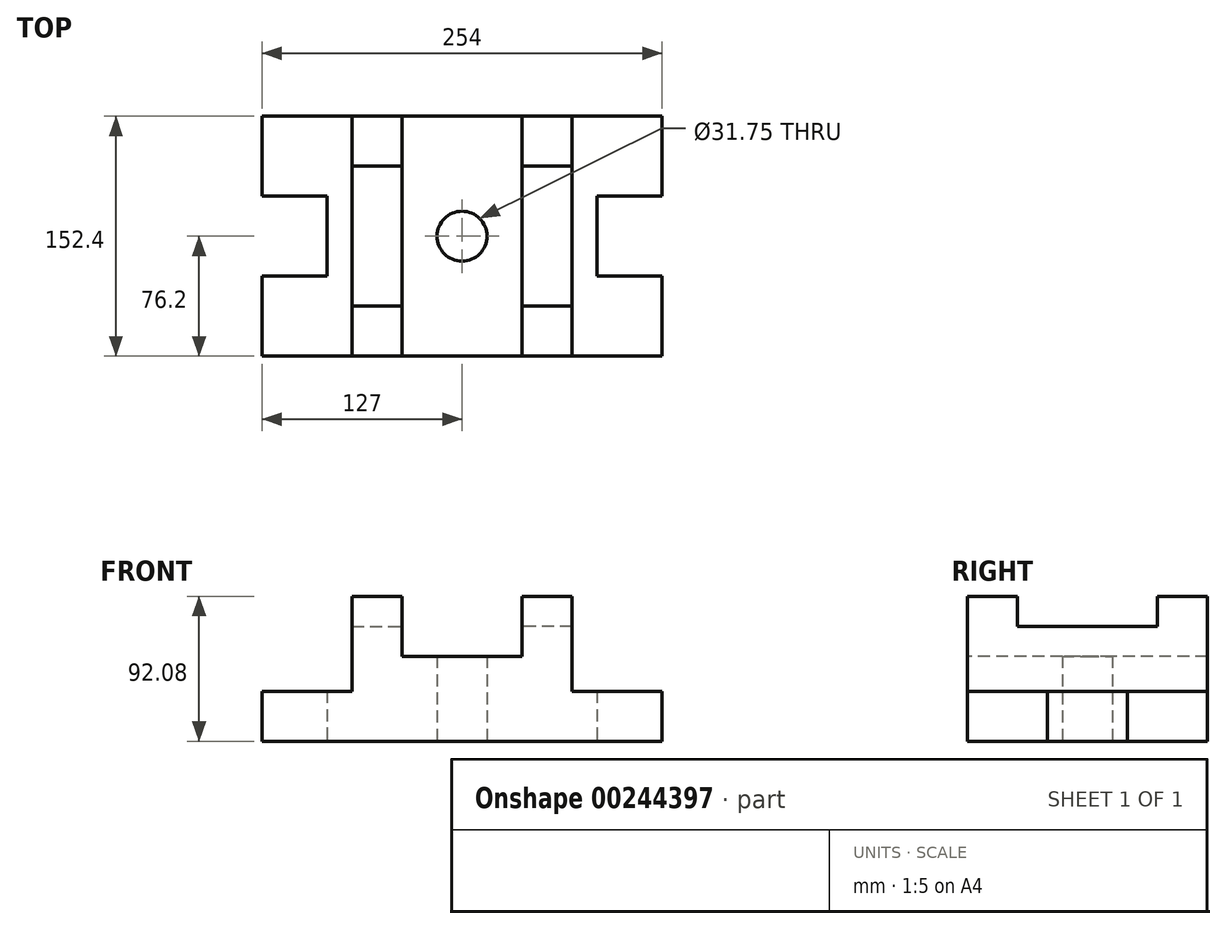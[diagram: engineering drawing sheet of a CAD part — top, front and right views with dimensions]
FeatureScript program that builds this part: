
annotation { "Feature Type Name" : "Feature", "Feature Type Description" : "" }
export const myFeature = defineFeature(function(context is Context, id is Id, definition is map)
    precondition{}
    {
        {
            var Q0;
            Q0=qCreatedBy(makeId("Top.planeOp"),FACE);
            var sketch = newSketch(context, id + "F0", { "sketchPlane" : qUnion([Q0])});
            skCircle(sketch, "E0", {"center": v(0, 0) * mm, "radius": 15.88 * mm});
            skLineSegment(sketch, "E1", {"start": v(0, 0) * mm, "end": v(0, -76.2) * mm});
            skLineSegment(sketch, "E2", {"start": v(0, -76.2) * mm, "end": v(127, -76.2) * mm});
            skLineSegment(sketch, "E3", {"start": v(127, -76.2) * mm, "end": v(127, -25.4) * mm});
            skLineSegment(sketch, "E4", {"start": v(127, -25.4) * mm, "end": v(85.72, -25.4) * mm});
            skLineSegment(sketch, "E5", {"start": v(85.72, -25.4) * mm, "end": v(85.72, 25.4) * mm});
            skLineSegment(sketch, "E6.MirrorCS", {"start": v(-85.72, -25.4) * mm, "end": v(-85.72, 25.4) * mm});
            skLineSegment(sketch, "E7.MirrorCS", {"start": v(-127, -76.2) * mm, "end": v(-127, -25.4) * mm});
            skLineSegment(sketch, "E8.MirrorCS", {"start": v(-127, -25.4) * mm, "end": v(-85.72, -25.4) * mm});
            skLineSegment(sketch, "E9.MirrorCS", {"start": v(0, -76.2) * mm, "end": v(-127, -76.2) * mm});
            skLineSegment(sketch, "E10.MirrorCS", {"start": v(-127, 25.4) * mm, "end": v(-85.72, 25.4) * mm});
            skLineSegment(sketch, "E11.MirrorCS", {"start": v(-127, 76.2) * mm, "end": v(-127, 25.4) * mm});
            skLineSegment(sketch, "E12.MirrorCS", {"start": v(0, 76.2) * mm, "end": v(-127, 76.2) * mm});
            skLineSegment(sketch, "E13.MirrorCS", {"start": v(0, 76.2) * mm, "end": v(127, 76.2) * mm});
            skLineSegment(sketch, "E14.MirrorCS", {"start": v(127, 76.2) * mm, "end": v(127, 25.4) * mm});
            skLineSegment(sketch, "E15.MirrorCS", {"start": v(127, 25.4) * mm, "end": v(85.72, 25.4) * mm});
            skLineSegment(sketch, "E16", {"start": v(-127, 76.2) * mm, "end": v(-69.85, 76.2) * mm});
            skLineSegment(sketch, "E17", {"start": v(-69.85, 76.2) * mm, "end": v(-69.85, 44.45) * mm});
            skLineSegment(sketch, "E18", {"start": v(-69.85, 44.45) * mm, "end": v(-38.1, 44.45) * mm});
            skLineSegment(sketch, "E19", {"start": v(-38.1, 44.45) * mm, "end": v(-38.1, 76.2) * mm});
            skLineSegment(sketch, "E20.MirrorCS", {"start": v(38.1, 44.45) * mm, "end": v(38.1, 76.2) * mm});
            skLineSegment(sketch, "E21.MirrorCS", {"start": v(69.85, 44.45) * mm, "end": v(38.1, 44.45) * mm});
            skLineSegment(sketch, "E22.MirrorCS", {"start": v(69.85, 76.2) * mm, "end": v(69.85, 44.45) * mm});
            skLineSegment(sketch, "E23.MirrorCS", {"start": v(69.85, -44.45) * mm, "end": v(38.1, -44.45) * mm});
            skLineSegment(sketch, "E24.MirrorCS", {"start": v(38.1, -44.45) * mm, "end": v(38.1, -76.2) * mm});
            skLineSegment(sketch, "E25.MirrorCS", {"start": v(69.85, -76.2) * mm, "end": v(69.85, -44.45) * mm});
            skLineSegment(sketch, "E26.MirrorCS", {"start": v(-38.1, -44.45) * mm, "end": v(-38.1, -76.2) * mm});
            skLineSegment(sketch, "E27.MirrorCS", {"start": v(-69.85, -44.45) * mm, "end": v(-38.1, -44.45) * mm});
            skLineSegment(sketch, "E28.MirrorCS", {"start": v(-69.85, -76.2) * mm, "end": v(-69.85, -44.45) * mm});
            skLineSegment(sketch, "E29", {"start": v(-69.85, 44.45) * mm, "end": v(-69.85, -44.45) * mm});
            skLineSegment(sketch, "E30", {"start": v(-38.1, 44.45) * mm, "end": v(-38.1, -44.45) * mm});
            skLineSegment(sketch, "E31", {"start": v(38.1, 44.45) * mm, "end": v(38.1, -44.45) * mm});
            skLineSegment(sketch, "E32", {"start": v(69.85, -44.45) * mm, "end": v(69.85, 44.45) * mm});
            skSolve(sketch);
        }
        {
            var Q0;
            Q0=makeQuery(id+"F0.imprint","IMPRINT",FACE,{"disambiguationData":[TD([[makeQuery(id+"F0.imprint","IMPRINT",EDGE,{"derivedFrom":sQuery(id+"F0.wireOp",EDGE,"E23.MirrorCS")}),1.0]])]});
            var Q1;
            {var subQ0=sQuery(id+"F0.wireOp",EDGE,"E26.MirrorCS");Q1=makeQuery(id+"F0.imprint","IMPRINT",FACE,{"disambiguationData":[TD([[makeQuery(id+"F0.imprint","IMPRINT",EDGE,{"derivedFrom":subQ0}),-1.0]])]});}
            var Q2;
            {var subQ0=sQuery(id+"F0.wireOp",EDGE,"E17");Q2=makeQuery(id+"F0.imprint","IMPRINT",FACE,{"disambiguationData":[TD([[makeQuery(id+"F0.imprint","IMPRINT",EDGE,{"derivedFrom":subQ0}),1.0]])]});}
            var Q3;
            {var subQ0=sQuery(id+"F0.wireOp",EDGE,"E20.MirrorCS");Q3=makeQuery(id+"F0.imprint","IMPRINT",FACE,{"disambiguationData":[TD([[makeQuery(id+"F0.imprint","IMPRINT",EDGE,{"derivedFrom":subQ0}),-1.0]])]});}
            extrude(context, id + "F1", {"entities" : qUnion([Q0, Q1, Q2, Q3]), "depth" : 92.07 * mm});
        }
        {
            var Q0;
            Q0=makeQuery(id+"F0.imprint","IMPRINT",FACE,{"disambiguationData":[TD([[makeQuery(id+"F0.imprint","IMPRINT",EDGE,{"derivedFrom":sQuery(id+"F0.wireOp",EDGE,"E6.MirrorCS")}),-1.0]])]});
            var Q1;
            {var subQ1=sQuery(id+"F0.wireOp",EDGE,"E3");Q1=makeQuery(id+"F0.imprint","IMPRINT",FACE,{"disambiguationData":[TD([[makeQuery(id+"F0.imprint","IMPRINT",EDGE,{"derivedFrom":subQ1}),1.0]])]});}
            extrude(context, id + "F2", {"entities" : qUnion([Q0, Q1]), "operationType" : NewBodyOperationType.ADD, "depth" : 31.75 * mm});
        }
        {
            var Q0;
            Q0=makeQuery(id+"F0.imprint","IMPRINT",FACE,{"disambiguationData":[TD([[makeQuery(id+"F0.imprint","IMPRINT",EDGE,{"derivedFrom":sQuery(id+"F0.wireOp",EDGE,"E0")}),-1.0]])]});
            extrude(context, id + "F3", {"entities" : qUnion([Q0]), "operationType" : NewBodyOperationType.ADD, "depth" : 53.97 * mm});
        }
        {
            var Q0;
            Q0=makeQuery(id+"F0.imprint","IMPRINT",FACE,{"disambiguationData":[TD([[makeQuery(id+"F0.imprint","IMPRINT",EDGE,{"derivedFrom":sQuery(id+"F0.wireOp",EDGE,"E18")}),-1.0]])]});
            var Q1;
            Q1=makeQuery(id+"F0.imprint","IMPRINT",FACE,{"disambiguationData":[TD([[makeQuery(id+"F0.imprint","IMPRINT",EDGE,{"derivedFrom":sQuery(id+"F0.wireOp",EDGE,"E21.MirrorCS")}),1.0]])]});
            extrude(context, id + "F4", {"entities" : qUnion([Q0, Q1]), "operationType" : NewBodyOperationType.ADD, "depth" : 73.02 * mm});
        }
    });
